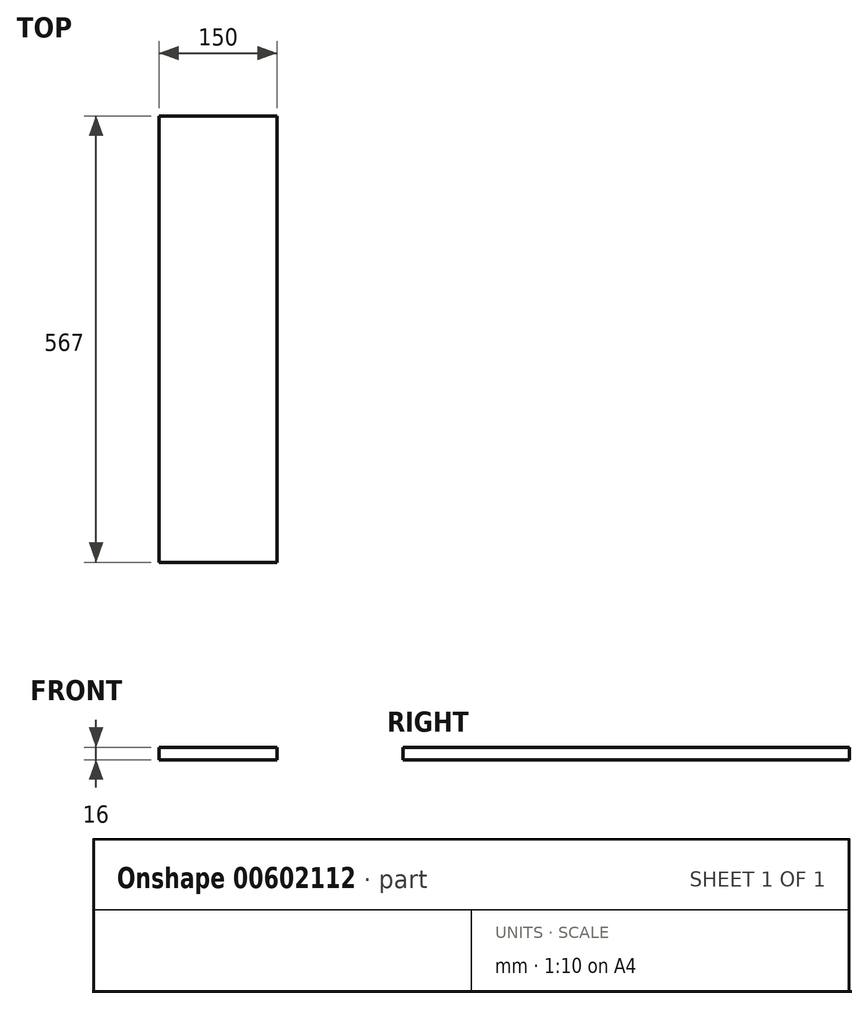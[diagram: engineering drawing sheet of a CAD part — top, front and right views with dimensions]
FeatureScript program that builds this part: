
annotation { "Feature Type Name" : "Feature", "Feature Type Description" : "" }
export const myFeature = defineFeature(function(context is Context, id is Id, definition is map)
    precondition{}
    {
        {
            var Q0;
            Q0=qCreatedBy(makeId("Top.planeOp"),FACE);
            var sketch = newSketch(context, id + "F0", { "sketchPlane" : qUnion([Q0])});
            skLineSegment(sketch, "E0.bottom", {"start": v(0, 0) * mm, "end": v(150, 0) * mm});
            skLineSegment(sketch, "E0.top", {"start": v(0, -567) * mm, "end": v(150, -567) * mm});
            skLineSegment(sketch, "E0.left", {"start": v(0, 0) * mm, "end": v(0, -567) * mm});
            skLineSegment(sketch, "E0.right", {"start": v(150, 0) * mm, "end": v(150, -567) * mm});
            skSolve(sketch);
        }
        {
            var Q0;
            Q0 = qSketchRegion(id + "F0", true);
            extrude(context, id + "F1", {"entities" : qUnion([Q0]), "depth" : 16 * mm, "offsetDistance" : 25 * mm});
        }
    });
